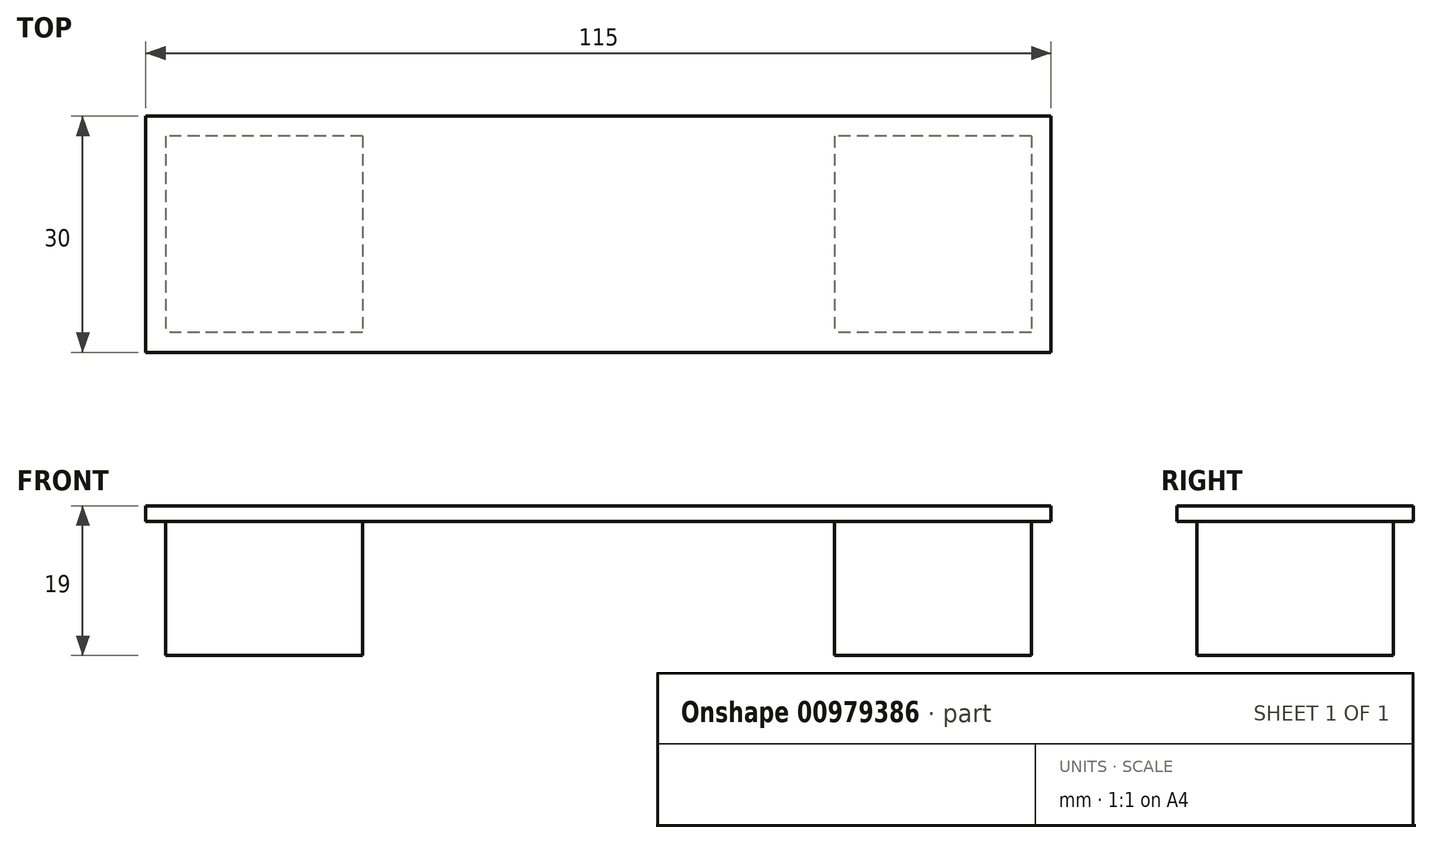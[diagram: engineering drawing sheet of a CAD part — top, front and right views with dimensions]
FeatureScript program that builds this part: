
annotation { "Feature Type Name" : "Feature", "Feature Type Description" : "" }
export const myFeature = defineFeature(function(context is Context, id is Id, definition is map)
    precondition{}
    {
        {
            var Q0;
            Q0=qCreatedBy(makeId("Top.planeOp"),FACE);
            var sketch = newSketch(context, id + "F0", { "sketchPlane" : qUnion([Q0])});
            skLineSegment(sketch, "E0.bottom", {"start": v(-59.85, 21.27) * mm, "end": v(55.15, 21.27) * mm});
            skLineSegment(sketch, "E0.top", {"start": v(-59.85, -8.73) * mm, "end": v(55.15, -8.73) * mm});
            skLineSegment(sketch, "E0.left", {"start": v(-59.85, 21.27) * mm, "end": v(-59.85, -8.73) * mm});
            skLineSegment(sketch, "E0.right", {"start": v(55.15, 21.27) * mm, "end": v(55.15, -8.73) * mm});
            skLineSegment(sketch, "E1", {"start": v(-59.85, -8.73) * mm, "end": v(-59.85, 6.27) * mm});
            skLineSegment(sketch, "E2", {"start": v(-59.85, 6.27) * mm, "end": v(55.15, 6.27) * mm});
            skLineSegment(sketch, "E3", {"start": v(-59.85, 6.27) * mm, "end": v(-44.85, 6.27) * mm});
            skLineSegment(sketch, "E4.bottom", {"start": v(-32.35, 18.77) * mm, "end": v(-57.35, 18.77) * mm});
            skLineSegment(sketch, "E4.top", {"start": v(-32.35, -6.23) * mm, "end": v(-57.35, -6.23) * mm});
            skLineSegment(sketch, "E4.left", {"start": v(-32.35, 18.77) * mm, "end": v(-32.35, -6.23) * mm});
            skLineSegment(sketch, "E4.right", {"start": v(-57.35, 18.77) * mm, "end": v(-57.35, -6.23) * mm});
            skPoint(sketch, "E4.middle", {"position": v(-44.85, 6.27) * mm});
            skLineSegment(sketch, "E5", {"start": v(55.15, 6.27) * mm, "end": v(40.15, 6.27) * mm});
            skLineSegment(sketch, "E6.bottom", {"start": v(52.65, 18.77) * mm, "end": v(27.65, 18.77) * mm});
            skLineSegment(sketch, "E6.top", {"start": v(52.65, -6.23) * mm, "end": v(27.65, -6.23) * mm});
            skLineSegment(sketch, "E6.left", {"start": v(52.65, 18.77) * mm, "end": v(52.65, -6.23) * mm});
            skLineSegment(sketch, "E6.right", {"start": v(27.65, 18.77) * mm, "end": v(27.65, -6.23) * mm});
            skPoint(sketch, "E6.middle", {"position": v(40.15, 6.27) * mm});
            skSolve(sketch);
        }
        {
            var Q0;
            Q0 = qSketchRegion(id + "F0", true);
            var Q1;
            {var subQ1=sQuery(id+"F0.wireOp",EDGE,"E4.bottom");Q1=makeQuery(id+"F0.imprint","IMPRINT",FACE,{"disambiguationData":[TD([[makeQuery(id+"F0.imprint","IMPRINT",EDGE,{"derivedFrom":subQ1}),1.0]])]});}
            var Q2;
            {var subQ1=sQuery(id+"F0.wireOp",EDGE,"E4.top");Q2=makeQuery(id+"F0.imprint","IMPRINT",FACE,{"disambiguationData":[TD([[makeQuery(id+"F0.imprint","IMPRINT",EDGE,{"derivedFrom":subQ1}),-1.0]])]});}
            var Q3;
            {var subQ1=sQuery(id+"F0.wireOp",EDGE,"E6.bottom");Q3=makeQuery(id+"F0.imprint","IMPRINT",FACE,{"disambiguationData":[TD([[makeQuery(id+"F0.imprint","IMPRINT",EDGE,{"derivedFrom":subQ1}),1.0]])]});}
            var Q4;
            {var subQ1=sQuery(id+"F0.wireOp",EDGE,"E6.top");Q4=makeQuery(id+"F0.imprint","IMPRINT",FACE,{"disambiguationData":[TD([[makeQuery(id+"F0.imprint","IMPRINT",EDGE,{"derivedFrom":subQ1}),-1.0]])]});}
            extrude(context, id + "F1", {"entities" : qUnion([Q0, Q1, Q2, Q3, Q4]), "oppositeDirection" : true, "depth" : 2 * mm, "offsetDistance" : 25 * mm});
        }
        {
            var Q0;
            {var subQ1=sQuery(id+"F0.wireOp",EDGE,"E4.top");Q0=makeQuery(id+"F0.imprint","IMPRINT",FACE,{"disambiguationData":[TD([[makeQuery(id+"F0.imprint","IMPRINT",EDGE,{"derivedFrom":subQ1}),-1.0]])]});}
            var Q1;
            {var subQ1=sQuery(id+"F0.wireOp",EDGE,"E4.bottom");Q1=makeQuery(id+"F0.imprint","IMPRINT",FACE,{"disambiguationData":[TD([[makeQuery(id+"F0.imprint","IMPRINT",EDGE,{"derivedFrom":subQ1}),1.0]])]});}
            var Q2;
            {var subQ1=sQuery(id+"F0.wireOp",EDGE,"E6.bottom");Q2=makeQuery(id+"F0.imprint","IMPRINT",FACE,{"disambiguationData":[TD([[makeQuery(id+"F0.imprint","IMPRINT",EDGE,{"derivedFrom":subQ1}),1.0]])]});}
            var Q3;
            {var subQ1=sQuery(id+"F0.wireOp",EDGE,"E6.top");Q3=makeQuery(id+"F0.imprint","IMPRINT",FACE,{"disambiguationData":[TD([[makeQuery(id+"F0.imprint","IMPRINT",EDGE,{"derivedFrom":subQ1}),-1.0]])]});}
            extrude(context, id + "F2", {"entities" : qUnion([Q0, Q1, Q2, Q3]), "operationType" : NewBodyOperationType.ADD, "oppositeDirection" : true, "depth" : 19 * mm, "offsetDistance" : 25 * mm});
        }
    });
